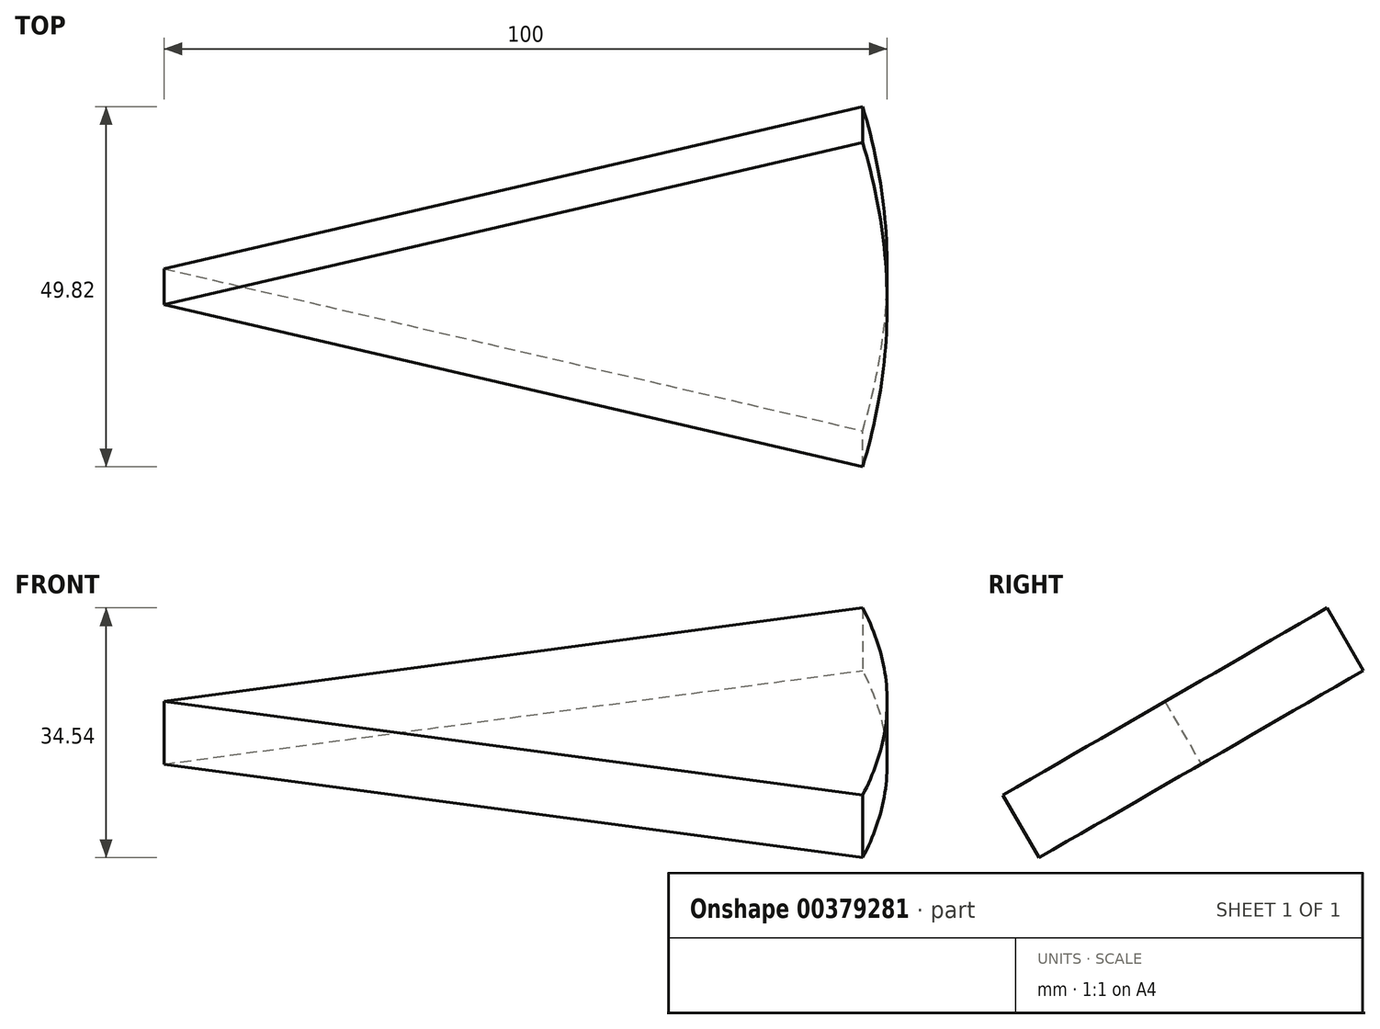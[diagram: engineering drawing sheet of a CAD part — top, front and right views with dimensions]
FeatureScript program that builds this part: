
annotation { "Feature Type Name" : "Feature", "Feature Type Description" : "" }
export const myFeature = defineFeature(function(context is Context, id is Id, definition is map)
    precondition{}
    {
        {
            var Q0;
            Q0=qCreatedBy(makeId("Top.planeOp"),FACE);
            var sketch = newSketch(context, id + "F0", { "sketchPlane" : qUnion([Q0])});
            skLineSegment(sketch, "E0", {"start": v(0, 0) * mm, "end": v(96.6, 25.88) * mm});
            skLineSegment(sketch, "E1", {"start": v(0, 0) * mm, "end": v(96.6, -25.88) * mm});
            skArc(sketch, "E2", {"start": v(96.6, 25.88) * mm, "mid": v(100, 0) * mm, "end": v(96.6, -25.88) * mm});
            skSolve(sketch);
        }
        {
            var Q0;
            Q0=makeQuery(id+"F0.imprint","IMPRINT",FACE,{"disambiguationData":[TD([[makeQuery(id+"F0.imprint","IMPRINT",EDGE,{"derivedFrom":sQuery(id+"F0.wireOp",EDGE,"E0")}),-1.0]])]});
            extrude(context, id + "F1", {"entities" : qUnion([Q0]), "depth" : 10 * mm});
        }
        {
            var Q0;
            Q0=qCreatedBy(makeId("Top.planeOp"),FACE);
            var sketch = newSketch(context, id + "F2", { "sketchPlane" : qUnion([Q0])});
            skLineSegment(sketch, "E3", {"start": v(0, 0) * mm, "end": v(120.8, 0) * mm, "construction": true});
            skSolve(sketch);
        }
        {
            var Q0;
            Q0=makeQuery(id+"F1.opExtrude","SWEPT_BODY",BODY,{"disambiguationData":[OSD([sQuery(id+"F0.wireOp",EDGE,"E0"),sQuery(id+"F0.wireOp",EDGE,"E1"),sQuery(id+"F0.wireOp",EDGE,"E2")])]});
            var Q1;
            Q1=sQuery(id+"F2.wireOp",EDGE,"E3");
            transform(context, id + "F3", {"entities" : qUnion([Q0]), "transformType" : TransformType.ROTATION, "transformAxis" : qUnion([Q1]), "angle" : 30 * degree, "makeCopy" : false});
        }
    });
